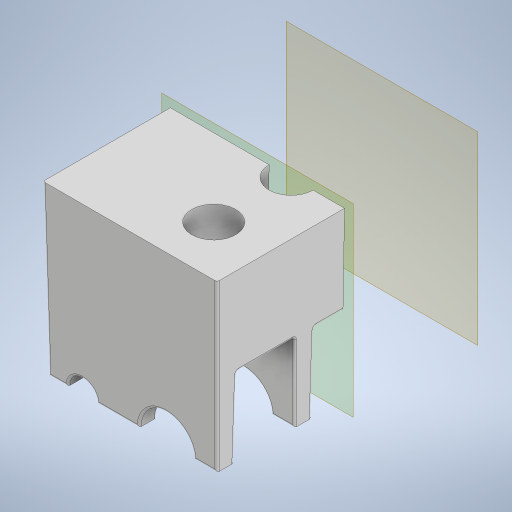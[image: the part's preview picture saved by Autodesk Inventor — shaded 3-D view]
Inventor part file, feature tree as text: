
AUTODESK INVENTOR PART (.ipt)
format: ipt  version: 2023 (Build 270158000, 158)  size: 750,592 bytes
history: native  units: in
note: dims shown in document units (in); Inventor stores cm internally (conversion verified against a paired STEP export)
features: draft x6, extrude x5, sketch x4, fillet x1, plane x1
ambient origin geometry x8: Origin, YZ Plane, XZ Plane, XY Plane, X Axis, Y Axis, Z Axis, Center Point
bodies: Solid1 (feature_tree)
feature tree (17):
  extrude  "Extrusion1"  Depth=5.0in
  sketch  "Sketch2"  dims[d3=7.4in d4=0.0in d6=1.4in]
  extrude  "Extrusion2"  Depth=1.4in
  extrude  "Extrusion3"  Depth=1.4in
  extrude  "Extrusion4"  Depth=0.0625in
  draft  "FaceDraft1"
  draft  "FaceDraft2"
  draft  "FaceDraft3"
  draft  "FaceDraft4"
  draft  "FaceDraft5"
  draft  "FaceDraft6"
  fillet  "Fillet1"  Radius=1.5in
  plane  "Work Plane1"
  extrude  "Extrusion5"  Depth=0.0625in
  sketch  "Sketch1"  dims[d0=5.0in d2=1.625in]
  sketch  "Sketch4"  dims[d7=1.5in d10=1.4in]
  sketch  "Sketch5"  dims[d11=1.5in d13=2.3in d14=1.5in d15=1.4in d16=3.7in d17=6.0in d18=0.5in d20=2.528in d21=7.4in d22=0.0in d23=7.4in d24=0.0in d25=1.5in d26=0.866in d27=1.5in d28=0.0in d29=1.4in d30=5.0in d31=-0.0069in d32=0.0069in d33=0.0069in d34=0.0069in d35=0.0069in d36=0.0069in d37=0.0625in d38=9.0in d39=0.0in]
